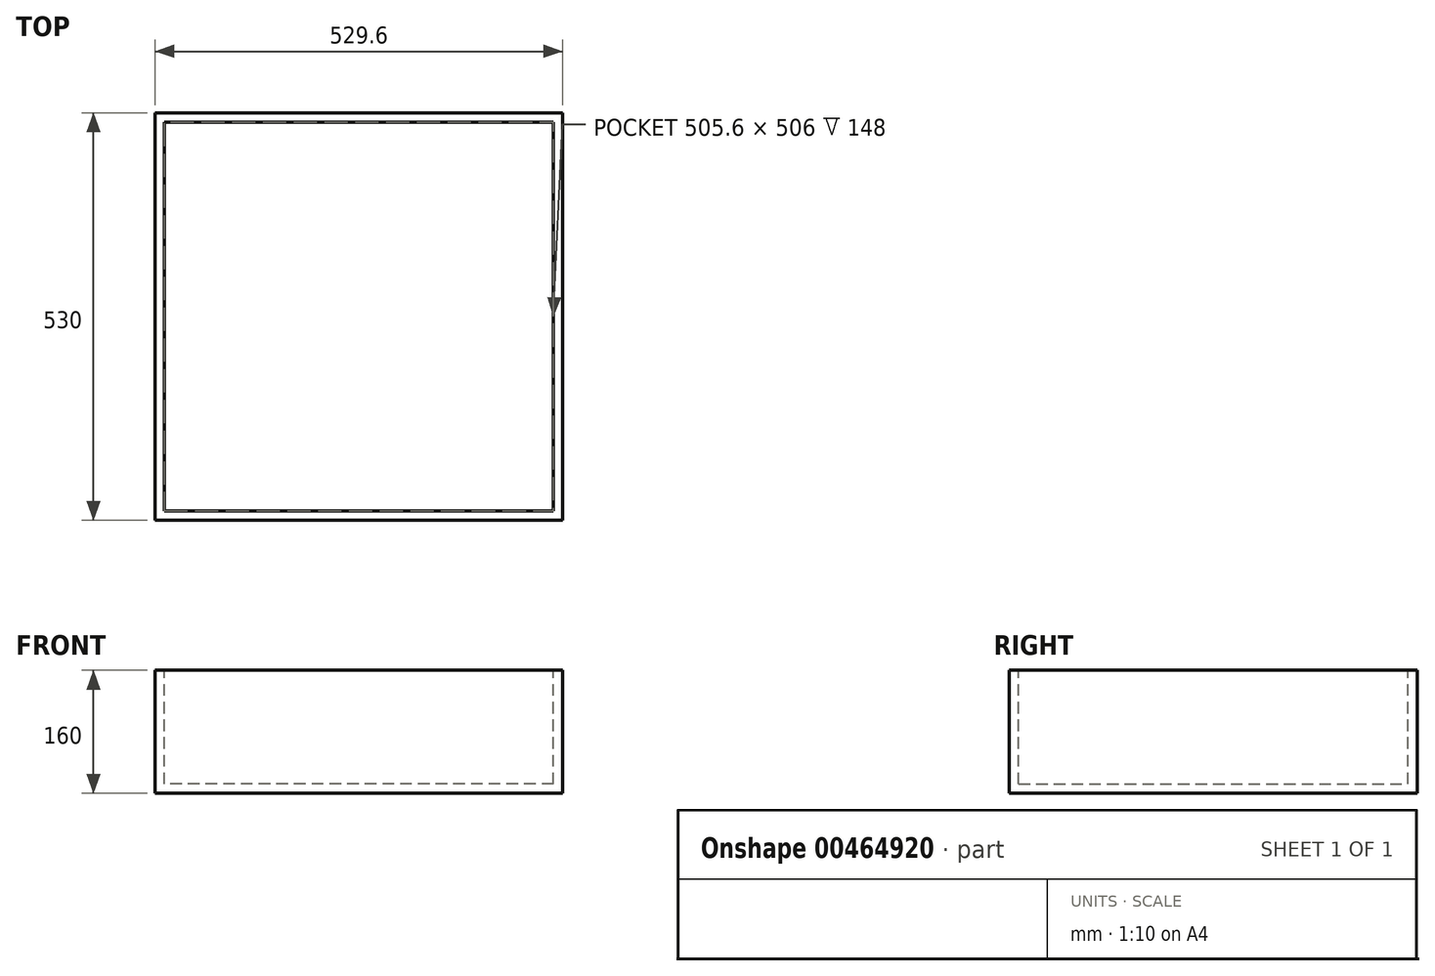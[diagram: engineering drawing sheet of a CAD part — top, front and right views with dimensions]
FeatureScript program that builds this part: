
annotation { "Feature Type Name" : "Feature", "Feature Type Description" : "" }
export const myFeature = defineFeature(function(context is Context, id is Id, definition is map)
    precondition{}
    {
        {
            var Q0;
            Q0=qCreatedBy(makeId("Front.planeOp"),FACE);
            var sketch = newSketch(context, id + "F0", { "sketchPlane" : qUnion([Q0])});
            skLineSegment(sketch, "E0.bottom", {"start": v(264.8, -80) * mm, "end": v(-264.8, -80) * mm});
            skLineSegment(sketch, "E0.top", {"start": v(264.8, 80) * mm, "end": v(-264.8, 80) * mm});
            skLineSegment(sketch, "E0.left", {"start": v(264.8, -80) * mm, "end": v(264.8, 80) * mm});
            skLineSegment(sketch, "E0.right", {"start": v(-264.8, -80) * mm, "end": v(-264.8, 80) * mm});
            skPoint(sketch, "E0.middle", {"position": v(0, 0) * mm});
            skSolve(sketch);
        }
        {
            var Q0;
            Q0=qSketchRegion(id+"F0",true);
            extrude(context, id + "F1", {"entities" : qUnion([Q0]), "depth" : 530 * mm, "offsetDistance" : 25 * mm});
        }
        {
            var Q0;
            Q0=makeQuery(id+"F1.opExtrude","SWEPT_FACE",FACE,{"disambiguationData":[OSD([sQuery(id+"F0.wireOp",EDGE,"E0.top")])]});
            shell(context, id + "F2", {"entities" : qUnion([Q0]), "thickness" : 12 * mm});
        }
    });
